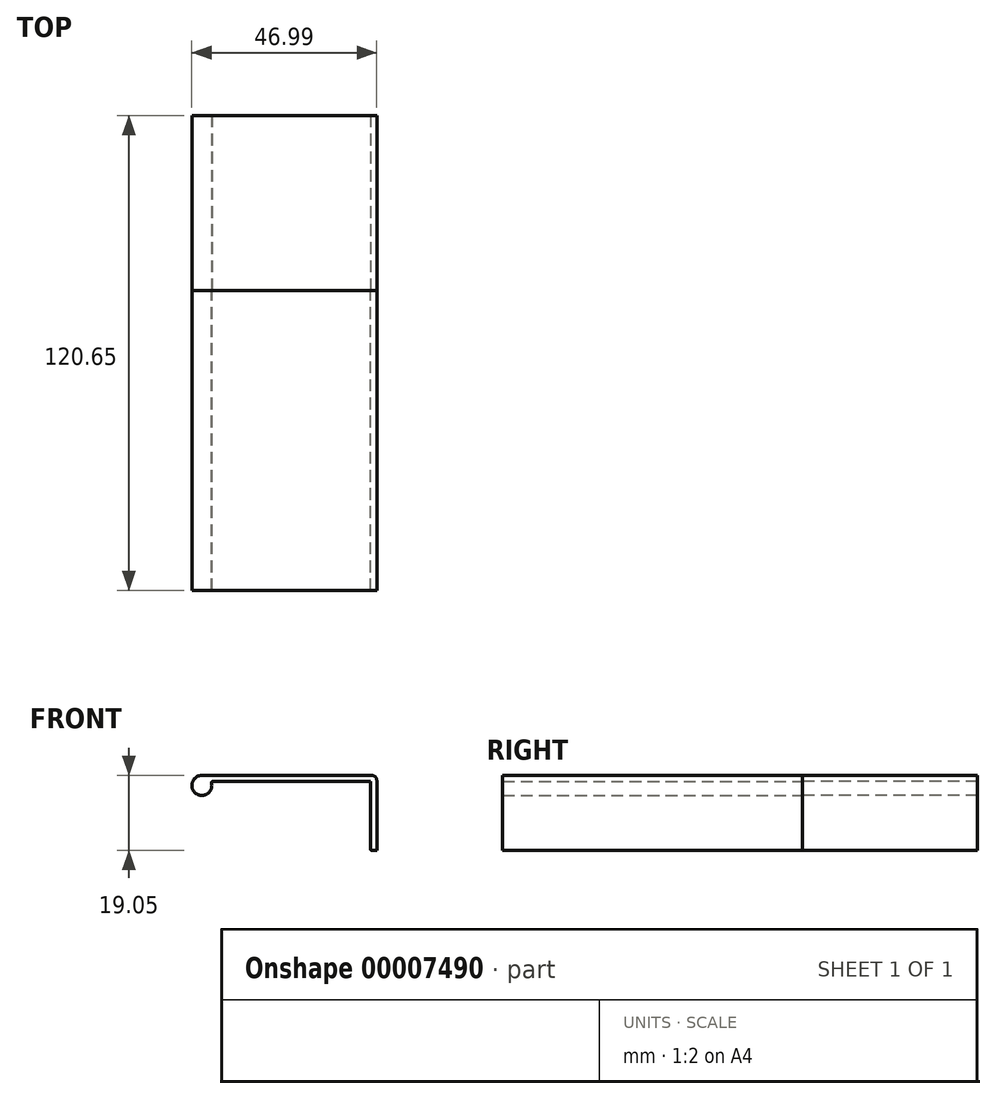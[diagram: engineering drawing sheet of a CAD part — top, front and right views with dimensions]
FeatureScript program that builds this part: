
annotation { "Feature Type Name" : "Feature", "Feature Type Description" : "" }
export const myFeature = defineFeature(function(context is Context, id is Id, definition is map)
    precondition{}
    {
        {
            var Q0;
            Q0=qCreatedBy(makeId("Front.planeOp"),FACE);
            var sketch = newSketch(context, id + "F0", { "sketchPlane" : qUnion([Q0])});
            skLineSegment(sketch, "E0", {"start": v(0, 0) * mm, "end": v(0, -17.2) * mm});
            skLineSegment(sketch, "E1", {"start": v(0.25, -17.46) * mm, "end": v(1.57, -17.46) * mm});
            skLineSegment(sketch, "E2", {"start": v(1.57, -17.46) * mm, "end": v(1.57, 0.32) * mm});
            skLineSegment(sketch, "E3", {"start": v(0.3, 1.59) * mm, "end": v(-42.88, 1.59) * mm});
            skLineSegment(sketch, "E4", {"start": v(0, 0) * mm, "end": v(-40.17, 0) * mm});
            skArc(sketch, "E5", {"start": v(-42.88, 1.59) * mm, "mid": v(-44.43, -2.96) * mm, "end": v(-40.42, -0.32) * mm});
            skPoint(sketch, "E6.visualSharp", {"position": v(1.57, 1.59) * mm});
            skArc(sketch, "E6.filletArc", {"start": v(1.57, 0.32) * mm, "mid": v(1.2, 1.22) * mm, "end": v(0.3, 1.59) * mm});
            skPoint(sketch, "E7.visualSharp", {"position": v(0, -17.46) * mm});
            skArc(sketch, "E7.filletArc", {"start": v(0, -17.2) * mm, "mid": v(0.07, -17.39) * mm, "end": v(0.25, -17.46) * mm});
            skPoint(sketch, "E8.visualSharp", {"position": v(-40.52, 0) * mm});
            skArc(sketch, "E8.filletArc", {"start": v(-40.17, 0) * mm, "mid": v(-40.37, -0.1) * mm, "end": v(-40.42, -0.32) * mm});
            skSolve(sketch);
        }
        {
            var Q0;
            Q0 = qSketchRegion(id + "F0", true);
            extrude(context, id + "F1", {"entities" : qUnion([Q0]), "oppositeDirection" : true, "depth" : 44.45 * mm});
        }
        {
            var Q0;
            Q0 = qSketchRegion(id + "F0", true);
            extrude(context, id + "F2", {"entities" : qUnion([Q0]), "depth" : 76.2 * mm});
        }
    });
